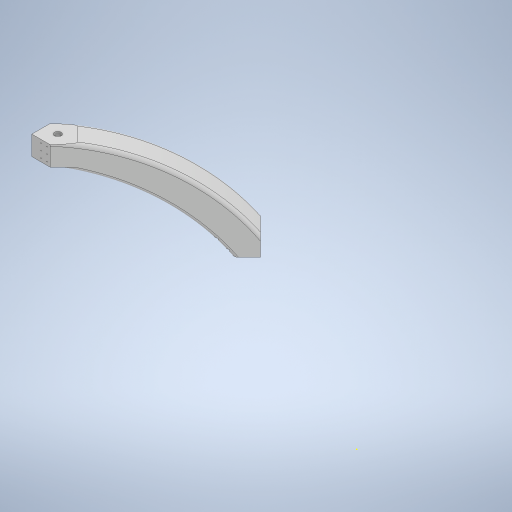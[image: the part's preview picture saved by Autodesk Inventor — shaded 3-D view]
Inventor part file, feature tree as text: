
AUTODESK INVENTOR PART (.ipt)
format: ipt  version: 2023 (Build 270158000, 158)  size: 477,696 bytes
history: native  units: in
note: dims shown in document units (in); Inventor stores cm internally (conversion verified against a paired STEP export)
features: other x16, sketch x9, extrude x8, hole x2, fillet x1
ambient origin geometry x8: Origin, YZ Plane, XZ Plane, XY Plane, X Axis, Y Axis, Z Axis, Center Point
bodies: Solid1 (feature_tree)
feature tree (36):
  sketch  "Sketch1"  dims[d0=54.0in d1=54.0in]
  sketch  "Sketch2"  dims[d2=1.0in d3=1.0in]
  extrude  "Extrusion1"  Depth=54.0in
  other  "Work Axis1"
  other  "Work Axis2"
  extrude  "Extrusion2"  Depth=1.0in
  sketch  "Sketch4"  dims[d36=0.25in d37=0.25in]
  extrude  "Extrusion3"  Depth=0.25in
  extrude  "Extrusion4"  Depth=0.25in
  extrude  "Extrusion5"  Depth=0.25in
  fillet  "Fillet1"  Radius=0.25in
  other  "Work Axis3"
  other  "Work Axis4"
  other  "Work Axis5"
  other  "Work Axis6"
  other  "Work Axis7"
  other  "Work Axis8"
  other  "Work Point2"
  other  "Work Point3"
  other  "Work Point4"
  other  "Work Point5"
  other  "Work Axis9"
  extrude  "Extrusion6"  Depth=2.0in
  extrude  "Extrusion7"  Depth=2.0in
  extrude  "Extrusion8"  Depth=12.0in
  other  "Work Point6"
  hole  "Hole1"  [1 undecoded]
  hole  "Hole2"  [1 undecoded]
  other  "Work Point1"
  sketch  "Sketch3"  dims[d34=0.25in d35=0.25in]
  sketch  "Sketch5"  dims[d38=0.25in d39=0.25in d40=0.25in]
  sketch  "Sketch6"  dims[d41=0.25in d42=2.0in]
  sketch  "Sketch7"  dims[d43=2.0in d44=2.0in]
  sketch  "Sketch8"  dims[d45=2.0in d46=12.0in]
  sketch  "Sketch9"  dims[d47=12.0in d48=12.0in d50=12.0in d51=15.0in d52=15.0in d53=15.0in d54=15.0in d55=15.0in d56=0.0in d57=3.0in d58=3.0in d59=3.0in d60=3.0in d61=30.0in d62=30.0in d63=15.0in d64=0.0in d65=0.125in d66=0.125in d67=0.125in d68=0.125in d69=0.125in d70=0.5in d71=1.414in d72=0.5in d73=0.5in d74=0.5in d75=0.5in d76=0.5in d77=1.414in d78=1.5in d79=1.414in d80=0.125in d81=0.125in d83=0.125in d84=0.125in d85=0.5in d86=0.5in d87=0.5in d88=1.414in d91=0.5in d92=0.5in d93=0.5in d94=1.414in d95=0.125in d96=1.5in d97=0.5in d98=0.125in d99=0.125in d100=1.414in d101=1.5in d102=1.5in d103=0.5in d104=1.0in d105=0.0in d106=1.0in d107=0.0in d108=0.25in d109=0.25in d110=0.25in d111=0.25in d112=0.25in d113=0.25in d114=0.75in d115=0.75in d116=2.0in d117=0.75in d118=0.75in d119=0.75in d120=0.75in d121=0.75in d122=2.0in d123=0.75in d124=0.75in d125=0.75in d126=10.0in d127=0.0in d128=0.5in d129=0.25in d130=0.25in d131=10.0in d132=0.0in d133=0.25in d134=2.0in d135=2.0in d136=1.0in d137=0.49in d138=0.0in d139=0.25in d140=3.0in d141=0.0in d142=1.0in d143=1.0in d144=1.0in d145=0.75in d146=0.375in d147=0.25in d148=0.5635in d149=1.0in d150=0.0in d151=1.0in d152=1.0in d153=1.0in d154=0.75in d155=0.375in d156=0.25in d157=0.5635in d158=1.0in d159=0.0in]
  other  "Work Axis10"
note: 2 required parameter values undecoded (feature->parameter linkage not recoverable at this tier; creation-order binding heuristic only, values carry confidence <= 0.55)
